# Revit family: ВКПІ_Eng
name_source: partatom
category: Mechanical Equipment
units: mm (PartAtom-declared; Revit-internal decimal feet)

## family parameters
Always vertical = Yes
Classification = None
Cut with Voids When Loaded = No
Part Type = Normal
Room Calculation Point = No
Round Connector Dimension = Use Diameter
Shared = No
Work Plane-Based = No

## types (8) — shared parameters
00_20_Manufacturer = Vents
00_20_Name = Centrifugal sound- and heat-insulated fan
Casing Material = Steel, galvanized
Description = For rectangular channels
Frequency = 50 Hz
Load Classification = HVAC
Maintenance zone material = <By Category>
Manufacturer = Vents
Number of Fase = 1
URL = https://ventilation-system.com
Voltage = 230 V
w = 50 mm  [stored 0.164042 ft]
zero-valued in all types: Default Elevation

## per-type parameters (varying)
| type | Amperage | Apparent Load | B | B1 | B2 | B3 | H | H1 | H2 | H3 | Height | L | Length | Maximum Air Flow | Power | Sound pressure level at 3 m distance | Temperature of moving air | Weight | Width | h | l | l1 |
| VKPI 2E 400х200 | 1 A | 138 VA | 400 mm  [stored 1.31234 ft] | 420 mm  [stored 1.37795 ft] | 440 mm  [stored 1.44357 ft] | 500 mm  [stored 1.64042 ft] | 200 mm  [stored 0.656168 ft] | 220 mm  [stored 0.721785 ft] | 240 mm  [stored 0.787402 ft] | 360 mm | 360 mm | 500 mm  [stored 1.64042 ft] | 500 mm  [stored 1.64042 ft] | 930.0 m³/h | 138 W | 45 dBA | -25...+45 °C | 24.50 kg | 500 mm  [stored 1.64042 ft] | 60 mm  [stored 0.19685 ft] | 150 mm | 100 mm  [stored 0.328084 ft] |
| VKPI 2E 500х250 | 1 A | 304 VA | 500 mm  [stored 1.64042 ft] | 520 mm  [stored 1.70604 ft] | 540 mm  [stored 1.77165 ft] | 600 mm | 250 mm  [stored 0.82021 ft] | 270 mm  [stored 0.885827 ft] | 290 mm  [stored 0.951444 ft] | 410 mm | 410 mm | 640 mm  [stored 2.09974 ft] | 640 mm  [stored 2.09974 ft] | 1720.0 m³/h | 305 W | 51 dBA | -25...+45 °C | 27.60 kg | 600 mm | 60 mm  [stored 0.19685 ft] | 200 mm  [stored 0.656168 ft] | 150 mm |
| VKPI 4E 500х300 | 1 A | 131 VA | 500 mm  [stored 1.64042 ft] | 520 mm  [stored 1.70604 ft] | 540 mm  [stored 1.77165 ft] | 600 mm | 300 mm | 320 mm  [stored 1.04987 ft] | 340 mm  [stored 1.11549 ft] | 460 mm | 460 mm | 680 mm  [stored 2.23097 ft] | 680 mm  [stored 2.23097 ft] | 1700.0 m³/h | 140 W | 48 dBA | -25...+45 °C | 37.20 kg | 600 mm | 60 mm  [stored 0.19685 ft] | 200 mm  [stored 0.656168 ft] | 150 mm |
| VKPI 4D 500х300 | 0 A | 78 VA | 500 mm  [stored 1.64042 ft] | 520 mm  [stored 1.70604 ft] | 540 mm  [stored 1.77165 ft] | 600 mm | 300 mm | 320 mm  [stored 1.04987 ft] | 340 mm  [stored 1.11549 ft] | 460 mm | 460 mm | 680 mm  [stored 2.23097 ft] | 680 mm  [stored 2.23097 ft] | 1380.0 m³/h | 136 W | 47 dBA | -25...+65 °C | 37.20 kg | 600 mm | 60 mm  [stored 0.19685 ft] | 200 mm  [stored 0.656168 ft] | 150 mm |
| VKPI 4E 600х300 | 1 A | 207 VA | 600 mm | 620 mm  [stored 2.03412 ft] | 640 mm  [stored 2.09974 ft] | 700 mm  [stored 2.29659 ft] | 300 mm | 320 mm  [stored 1.04987 ft] | 340 mm  [stored 1.11549 ft] | 460 mm | 460 mm | 680 mm  [stored 2.23097 ft] | 680 mm  [stored 2.23097 ft] | 2470.0 m³/h | 220 W | 46 dBA | -25...+45 °C | 43.50 kg | 700 mm  [stored 2.29659 ft] | 60 mm  [stored 0.19685 ft] | 250 mm  [stored 0.82021 ft] | 200 mm  [stored 0.656168 ft] |
| VKPI 4D 600х300 | 1 A | 120 VA | 600 mm | 620 mm  [stored 2.03412 ft] | 640 mm  [stored 2.09974 ft] | 700 mm  [stored 2.29659 ft] | 300 mm | 320 mm  [stored 1.04987 ft] | 340 mm  [stored 1.11549 ft] | 460 mm | 460 mm | 680 mm  [stored 2.23097 ft] | 680 mm  [stored 2.23097 ft] | 2530.0 m³/h | 230 W | 45 dBA | -25...+70 °C | 43.50 kg | 700 mm  [stored 2.29659 ft] | 60 mm  [stored 0.19685 ft] | 250 mm  [stored 0.82021 ft] | 200 mm  [stored 0.656168 ft] |
| VKPI 4E 600х350 | 2 A | 545 VA | 600 mm | 620 mm  [stored 2.03412 ft] | 640 mm  [stored 2.09974 ft] | 700 mm  [stored 2.29659 ft] | 350 mm  [stored 1.14829 ft] | 370 mm  [stored 1.21391 ft] | 390 mm  [stored 1.27953 ft] | 530 mm  [stored 1.73885 ft] | 530 mm  [stored 1.73885 ft] | 735 mm | 735 mm | 2950.0 m³/h | 470 W | 47 dBA | -40...+80 °C | 56.20 kg | 700 mm  [stored 2.29659 ft] | 70 mm  [stored 0.229659 ft] | 250 mm  [stored 0.82021 ft] | 200 mm  [stored 0.656168 ft] |
| VKPI 4D 600х350 | 1 A | 324 VA | 600 mm | 620 mm  [stored 2.03412 ft] | 640 mm  [stored 2.09974 ft] | 700 mm  [stored 2.29659 ft] | 350 mm  [stored 1.14829 ft] | 370 mm  [stored 1.21391 ft] | 390 mm  [stored 1.27953 ft] | 530 mm  [stored 1.73885 ft] | 530 mm  [stored 1.73885 ft] | 735 mm | 735 mm | 2970.0 m³/h | 510 W | 46 dBA | -40...+60 °C | 56.20 kg | 700 mm  [stored 2.29659 ft] | 70 mm  [stored 0.229659 ft] | 250 mm  [stored 0.82021 ft] | 200 mm  [stored 0.656168 ft] |

note: column(s) folded — value = type name in every type: 00_20_Type

note: [stored X ft] marks values corroborated as IEEE doubles in the binary element streams (Revit-internal decimal feet)
